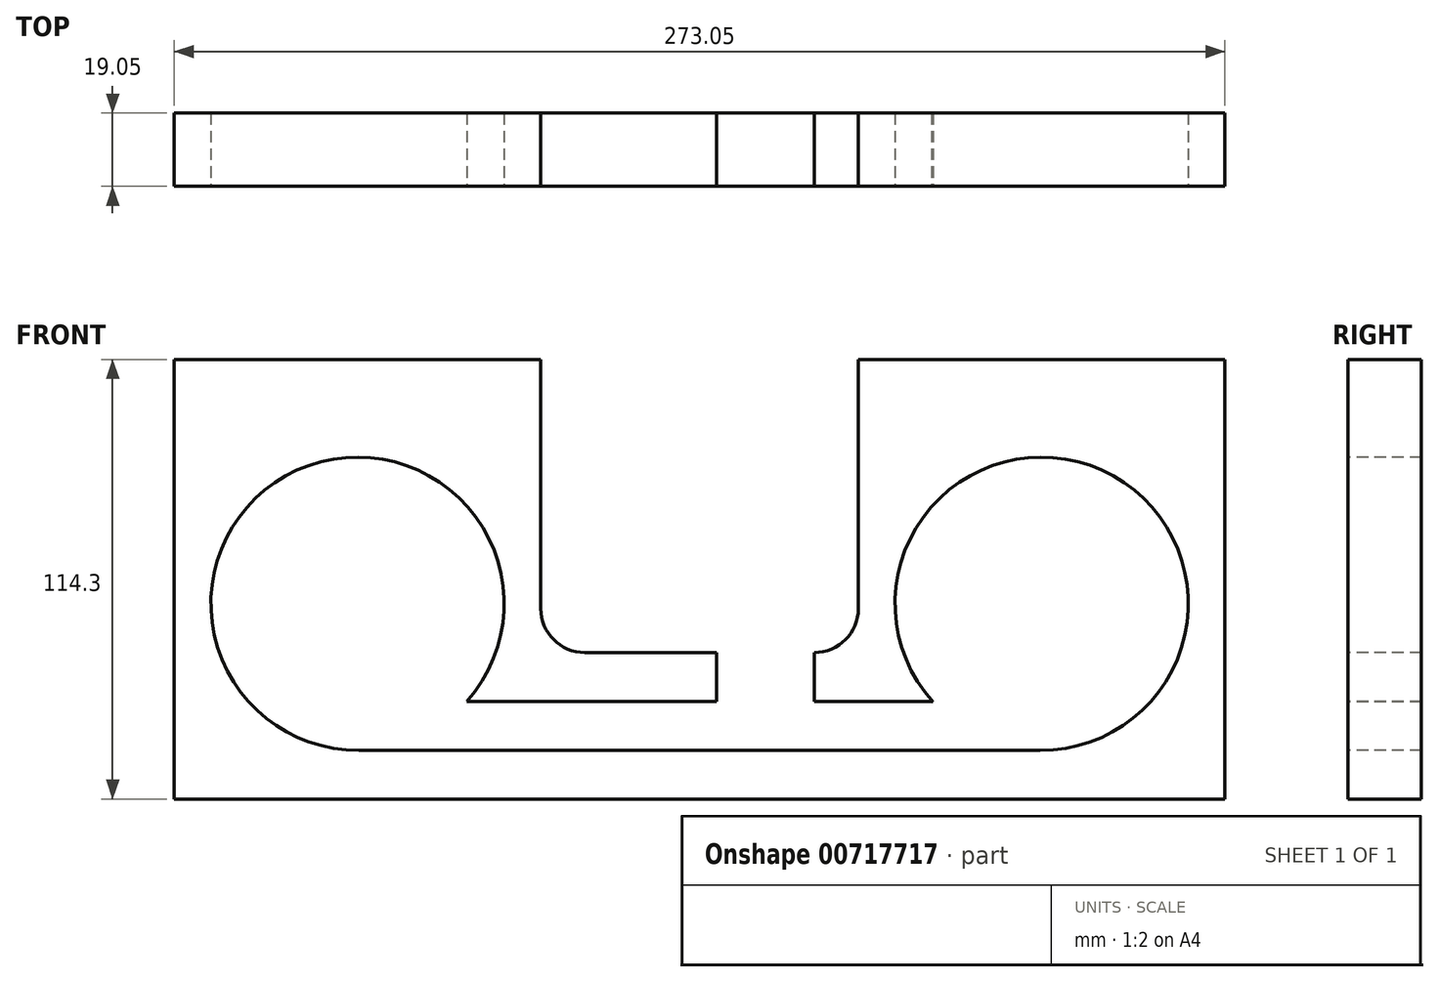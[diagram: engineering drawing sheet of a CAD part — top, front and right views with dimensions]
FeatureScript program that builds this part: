
annotation { "Feature Type Name" : "Feature", "Feature Type Description" : "" }
export const myFeature = defineFeature(function(context is Context, id is Id, definition is map)
    precondition{}
    {
        {
            var Q0;
            Q0=qCreatedBy(makeId("Front.planeOp"),FACE);
            var sketch = newSketch(context, id + "F0", { "sketchPlane" : qUnion([Q0])});
            skLineSegment(sketch, "E0.bottom", {"start": v(0, 0) * mm, "end": v(273.05, 0) * mm});
            skLineSegment(sketch, "E0.top", {"start": v(0, 114.3) * mm, "end": v(273.05, 114.3) * mm});
            skLineSegment(sketch, "E0.left", {"start": v(0, 0) * mm, "end": v(0, 114.3) * mm});
            skLineSegment(sketch, "E0.right", {"start": v(273.05, 0) * mm, "end": v(273.05, 114.3) * mm});
            skSolve(sketch);
        }
        {
            var Q0;
            Q0=qSketchRegion(id+"F0",true);
            extrude(context, id + "F1", {"entities" : qUnion([Q0]), "depth" : 19.05 * mm, "offsetDistance" : 25.4 * mm});
        }
        {
            var Q0;
            Q0=makeQuery(id+"F1.opExtrude","CAP_FACE",FACE,{"disambiguationData":[OSD([sQuery(id+"F0.wireOp",EDGE,"E0.bottom"),sQuery(id+"F0.wireOp",EDGE,"E0.top"),sQuery(id+"F0.wireOp",EDGE,"E0.left"),sQuery(id+"F0.wireOp",EDGE,"E0.right")])],"isStart":false});
            var sketch = newSketch(context, id + "F2", { "sketchPlane" : qUnion([Q0])});
            skCircle(sketch, "E1", {"center": v(47.63, 50.8) * mm, "radius": 38.1 * mm});
            skCircle(sketch, "E2", {"center": v(225.43, 50.8) * mm, "radius": 38.1 * mm});
            skSolve(sketch);
        }
        {
            var Q0;
            Q0 = qSketchRegion(id + "F2", true);
            extrude(context, id + "F3", {"entities" : qUnion([Q0]), "operationType" : NewBodyOperationType.REMOVE, "oppositeDirection" : true, "depth" : 25.4 * mm, "offsetDistance" : 25.4 * mm});
        }
        {
            var Q0;
            Q0=makeQuery(id+"F1.opExtrude","CAP_FACE",FACE,{"disambiguationData":[OSD([sQuery(id+"F0.wireOp",EDGE,"E0.bottom"),sQuery(id+"F0.wireOp",EDGE,"E0.top"),sQuery(id+"F0.wireOp",EDGE,"E0.left"),sQuery(id+"F0.wireOp",EDGE,"E0.right")])],"isStart":false});
            var sketch = newSketch(context, id + "F4", { "sketchPlane" : qUnion([Q0])});
            skLineSegment(sketch, "E3", {"start": v(95.25, 114.3) * mm, "end": v(95.25, 49.53) * mm});
            skLineSegment(sketch, "E4", {"start": v(106.68, 38.1) * mm, "end": v(166.37, 38.1) * mm});
            skLineSegment(sketch, "E5", {"start": v(177.8, 49.53) * mm, "end": v(177.8, 114.3) * mm});
            skPoint(sketch, "E6.visualSharp", {"position": v(95.25, 38.1) * mm});
            skArc(sketch, "E6.filletArc", {"start": v(95.25, 49.53) * mm, "mid": v(98.6, 41.45) * mm, "end": v(106.68, 38.1) * mm});
            skPoint(sketch, "E7.visualSharp", {"position": v(177.8, 38.1) * mm});
            skArc(sketch, "E7.filletArc", {"start": v(166.37, 38.1) * mm, "mid": v(174.45, 41.45) * mm, "end": v(177.8, 49.53) * mm});
            skSolve(sketch);
        }
        {
            var Q0;
            Q0 = qSketchRegion(id + "F4", true);
            var Q1;
            {var subQ1=sQuery(id+"F4.wireOp",EDGE,"E3");Q1=makeQuery(id+"F4.imprint","IMPRINT",FACE,{"disambiguationData":[TD([[makeQuery(id+"F4.imprint","IMPRINT",EDGE,{"derivedFrom":subQ1}),1.0]])]});}
            extrude(context, id + "F5", {"entities" : qUnion([Q0, Q1]), "operationType" : NewBodyOperationType.REMOVE, "oppositeDirection" : true, "depth" : 45.72 * mm, "offsetDistance" : 25.4 * mm});
        }
        {
            var Q0;
            Q0=makeQuery(id+"F1.opExtrude","CAP_FACE",FACE,{"disambiguationData":[OSD([sQuery(id+"F0.wireOp",EDGE,"E0.bottom"),sQuery(id+"F0.wireOp",EDGE,"E0.top"),sQuery(id+"F0.wireOp",EDGE,"E0.left"),sQuery(id+"F0.wireOp",EDGE,"E0.right")])],"isStart":false});
            var sketch = newSketch(context, id + "F6", { "sketchPlane" : qUnion([Q0])});
            skLineSegment(sketch, "E8", {"start": v(166.37, 38.1) * mm, "end": v(140.97, 38.1) * mm});
            skLineSegment(sketch, "E9", {"start": v(140.97, 38.1) * mm, "end": v(140.97, 25.4) * mm});
            skLineSegment(sketch, "E10", {"start": v(140.97, 25.4) * mm, "end": v(59.76, 25.4) * mm});
            skLineSegment(sketch, "E11", {"start": v(196.84, 25.4) * mm, "end": v(166.37, 25.4) * mm});
            skLineSegment(sketch, "E12", {"start": v(166.37, 25.4) * mm, "end": v(166.37, 38.1) * mm});
            skLineSegment(sketch, "E13", {"start": v(59.76, 25.4) * mm, "end": v(48, 12.7) * mm});
            skLineSegment(sketch, "E14", {"start": v(48, 12.7) * mm, "end": v(225.8, 12.7) * mm});
            skLineSegment(sketch, "E15", {"start": v(225.8, 12.7) * mm, "end": v(196.84, 25.4) * mm});
            skSolve(sketch);
        }
        {
            var Q0;
            Q0 = qSketchRegion(id + "F6", true);
            extrude(context, id + "F7", {"entities" : qUnion([Q0]), "operationType" : NewBodyOperationType.REMOVE, "oppositeDirection" : true, "depth" : 25.4 * mm, "offsetDistance" : 25.4 * mm});
        }
    });
